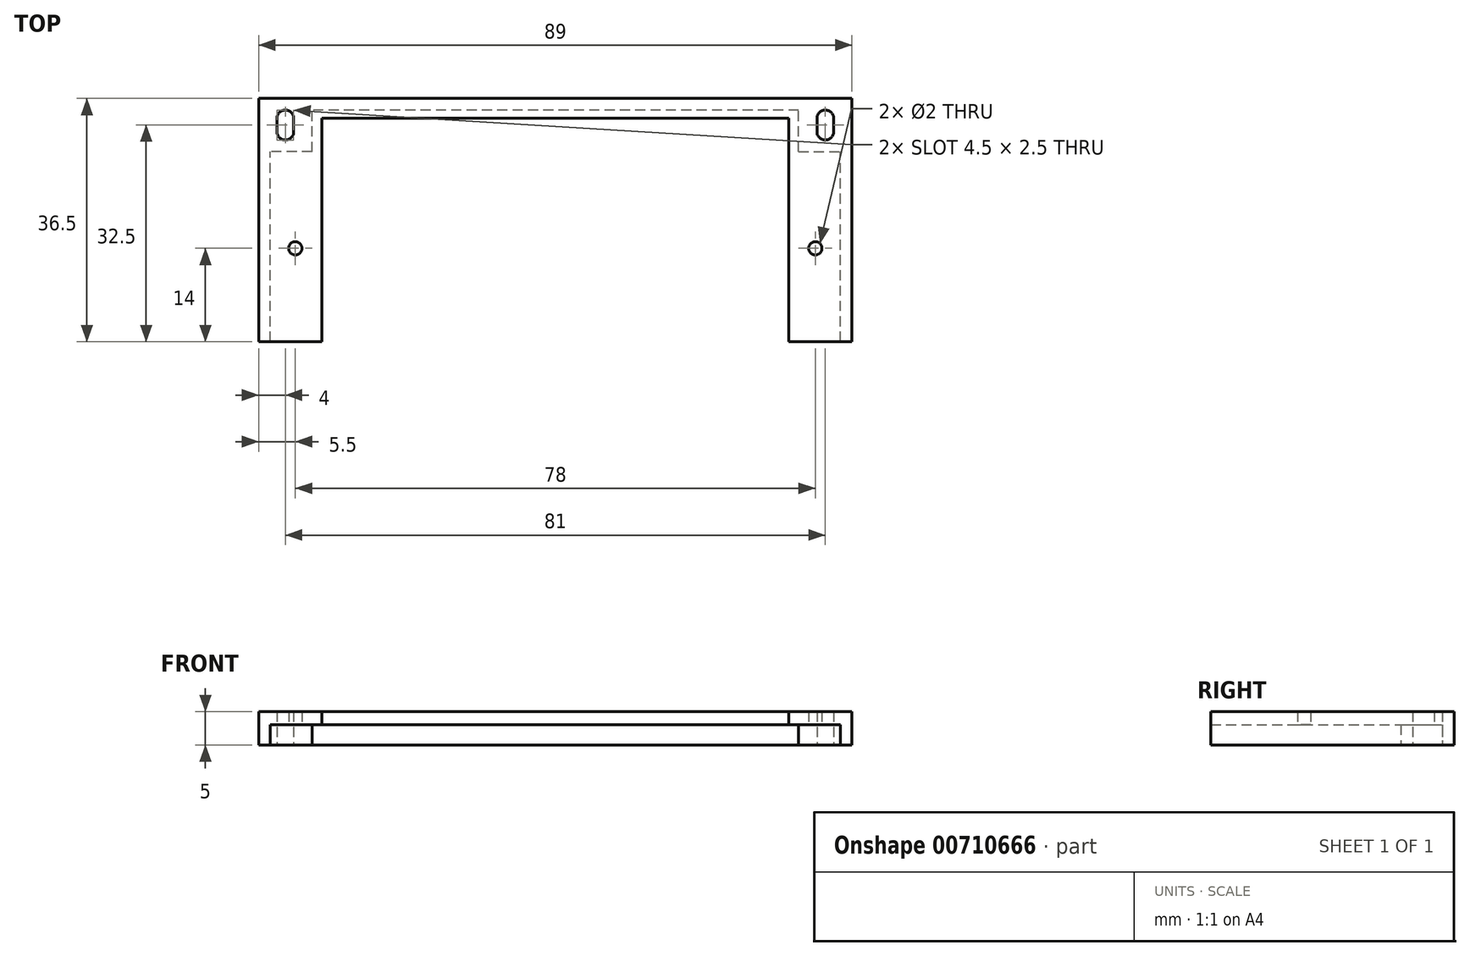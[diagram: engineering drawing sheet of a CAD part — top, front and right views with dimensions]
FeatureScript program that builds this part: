
annotation { "Feature Type Name" : "Feature", "Feature Type Description" : "" }
export const myFeature = defineFeature(function(context is Context, id is Id, definition is map)
    precondition{}
    {
        {
            var Q0;
            Q0=qCreatedBy(makeId("Top.planeOp"),FACE);
            var sketch = newSketch(context, id + "F0", { "sketchPlane" : qUnion([Q0])});
            skLineSegment(sketch, "E0.bottom", {"start": v(44.5, -22.5) * mm, "end": v(-44.5, -22.5) * mm});
            skLineSegment(sketch, "E0.top", {"start": v(44.5, 22.5) * mm, "end": v(-44.5, 22.5) * mm});
            skLineSegment(sketch, "E0.left", {"start": v(44.5, -22.5) * mm, "end": v(44.5, 22.5) * mm});
            skLineSegment(sketch, "E0.right", {"start": v(-44.5, -22.5) * mm, "end": v(-44.5, 22.5) * mm});
            skPoint(sketch, "E0.middle", {"position": v(0, 0) * mm});
            skSolve(sketch);
        }
        {
            var Q0;
            Q0=qSketchRegion(id+"F0",true);
            extrude(context, id + "F1", {"entities" : qUnion([Q0]), "depth" : 5 * mm, "offsetDistance" : 25 * mm});
        }
        {
            var Q0;
            Q0=qCreatedBy(makeId("Top.planeOp"),FACE);
            var sketch = newSketch(context, id + "F2", { "sketchPlane" : qUnion([Q0])});
            skLineSegment(sketch, "E1.bottom", {"start": v(35, -19.5) * mm, "end": v(-35, -19.5) * mm});
            skLineSegment(sketch, "E1.top", {"start": v(35, 19.5) * mm, "end": v(-35, 19.5) * mm});
            skLineSegment(sketch, "E1.left", {"start": v(35, -19.5) * mm, "end": v(35, 19.5) * mm});
            skLineSegment(sketch, "E1.right", {"start": v(-35, -19.5) * mm, "end": v(-35, 19.5) * mm});
            skPoint(sketch, "E1.middle", {"position": v(0, 0) * mm});
            skSolve(sketch);
        }
        {
            var Q0;
            Q0=qSketchRegion(id+"F2",true);
            extrude(context, id + "F3", {"entities" : qUnion([Q0]), "operationType" : NewBodyOperationType.REMOVE, "depth" : 25 * mm, "offsetDistance" : 25 * mm});
        }
        {
            var Q0;
            Q0=qCreatedBy(makeId("Top.planeOp"),FACE);
            var sketch = newSketch(context, id + "F4", { "sketchPlane" : qUnion([Q0])});
            skLineSegment(sketch, "E2.bottom", {"start": v(42.75, -20.75) * mm, "end": v(-42.75, -20.75) * mm});
            skLineSegment(sketch, "E2.top", {"start": v(42.75, 20.75) * mm, "end": v(-42.75, 20.75) * mm});
            skLineSegment(sketch, "E2.left", {"start": v(42.75, -20.75) * mm, "end": v(42.75, 20.75) * mm});
            skLineSegment(sketch, "E2.right", {"start": v(-42.75, -20.75) * mm, "end": v(-42.75, 20.75) * mm});
            skPoint(sketch, "E2.middle", {"position": v(0, 0) * mm});
            skSolve(sketch);
        }
        {
            var Q0;
            Q0=qSketchRegion(id+"F4",true);
            extrude(context, id + "F5", {"entities" : qUnion([Q0]), "operationType" : NewBodyOperationType.REMOVE, "depth" : 3 * mm, "offsetDistance" : 25 * mm});
        }
        {
            var Q0;
            Q0=qCreatedBy(makeId("Top.planeOp"),FACE);
            var sketch = newSketch(context, id + "F6", { "sketchPlane" : qUnion([Q0])});
            skLineSegment(sketch, "E3.bottom", {"start": v(-36.5, 14.5) * mm, "end": v(-44.5, 14.5) * mm});
            skLineSegment(sketch, "E3.top", {"start": v(-36.5, 22.5) * mm, "end": v(-44.5, 22.5) * mm});
            skLineSegment(sketch, "E3.left", {"start": v(-36.5, 14.5) * mm, "end": v(-36.5, 22.5) * mm});
            skLineSegment(sketch, "E3.right", {"start": v(-44.5, 14.5) * mm, "end": v(-44.5, 22.5) * mm});
            skPoint(sketch, "E3.middle", {"position": v(-40.5, 18.5) * mm});
            skLineSegment(sketch, "E4.bottom", {"start": v(-44.5, -22.5) * mm, "end": v(-36.5, -22.5) * mm});
            skLineSegment(sketch, "E4.top", {"start": v(-44.5, -14.5) * mm, "end": v(-36.5, -14.5) * mm});
            skLineSegment(sketch, "E4.left", {"start": v(-44.5, -22.5) * mm, "end": v(-44.5, -14.5) * mm});
            skLineSegment(sketch, "E4.right", {"start": v(-36.5, -22.5) * mm, "end": v(-36.5, -14.5) * mm});
            skPoint(sketch, "E4.middle", {"position": v(-40.5, -18.5) * mm});
            skLineSegment(sketch, "E5.bottom", {"start": v(36.5, 14.5) * mm, "end": v(44.5, 14.5) * mm});
            skLineSegment(sketch, "E5.top", {"start": v(36.5, 22.5) * mm, "end": v(44.5, 22.5) * mm});
            skLineSegment(sketch, "E5.left", {"start": v(36.5, 14.5) * mm, "end": v(36.5, 22.5) * mm});
            skLineSegment(sketch, "E5.right", {"start": v(44.5, 14.5) * mm, "end": v(44.5, 22.5) * mm});
            skPoint(sketch, "E5.middle", {"position": v(40.5, 18.5) * mm});
            skLineSegment(sketch, "E6.bottom", {"start": v(44.5, -14.5) * mm, "end": v(36.5, -14.5) * mm});
            skLineSegment(sketch, "E6.top", {"start": v(44.5, -22.5) * mm, "end": v(36.5, -22.5) * mm});
            skLineSegment(sketch, "E6.left", {"start": v(44.5, -14.5) * mm, "end": v(44.5, -22.5) * mm});
            skLineSegment(sketch, "E6.right", {"start": v(36.5, -14.5) * mm, "end": v(36.5, -22.5) * mm});
            skSolve(sketch);
        }
        {
            var Q0;
            Q0=qSketchRegion(id+"F6",true);
            extrude(context, id + "F7", {"entities" : qUnion([Q0]), "operationType" : NewBodyOperationType.ADD, "depth" : 3 * mm, "offsetDistance" : 25 * mm});
        }
        {
            var Q0;
            Q0=qCreatedBy(makeId("Top.planeOp"),FACE);
            var sketch = newSketch(context, id + "F8", { "sketchPlane" : qUnion([Q0])});
            skCircle(sketch, "E7", {"center": v(40.5, 19.5) * mm, "radius": 1.25 * mm});
            skCircle(sketch, "E8", {"center": v(-40.5, 19.5) * mm, "radius": 1.25 * mm});
            skCircle(sketch, "E9", {"center": v(-39, 0) * mm, "radius": 1 * mm});
            skCircle(sketch, "E10", {"center": v(39, 0) * mm, "radius": 1 * mm});
            skCircle(sketch, "E11.1.0.0", {"center": v(-40.5, 17.5) * mm, "radius": 1.25 * mm});
            skLineSegment(sketch, "E11.direction1", {"start": v(-40.5, 19.5) * mm, "end": v(-40.5, 17.5) * mm, "construction": true});
            skCircle(sketch, "E12.1.0.0", {"center": v(40.5, 17.5) * mm, "radius": 1.25 * mm});
            skLineSegment(sketch, "E12.direction1", {"start": v(40.5, 19.5) * mm, "end": v(40.5, 17.5) * mm, "construction": true});
            skSolve(sketch);
        }
        {
            var Q0;
            Q0=qSketchRegion(id+"F8",true);
            extrude(context, id + "F9", {"entities" : qUnion([Q0]), "operationType" : NewBodyOperationType.REMOVE, "depth" : 25 * mm, "offsetDistance" : 25 * mm});
        }
        {
            var Q0;
            Q0=qSketchRegion(id+"F8",true);
            extrude(context, id + "F10", {"entities" : qUnion([Q0]), "operationType" : NewBodyOperationType.REMOVE, "depth" : 25 * mm, "offsetDistance" : 25 * mm});
        }
        {
            var Q0;
            Q0=makeQuery(id+"F7.boolean.opBoolean","MERGE",FACE,{"derivedFrom":[makeQuery(id+"F1.opExtrude","CAP_FACE",FACE,{"disambiguationData":[OSD([sQuery(id+"F0.wireOp",EDGE,"E0.bottom"),sQuery(id+"F0.wireOp",EDGE,"E0.top"),sQuery(id+"F0.wireOp",EDGE,"E0.left"),sQuery(id+"F0.wireOp",EDGE,"E0.right")])],"isStart":true}),makeQuery(id+"F7.opExtrude","CAP_FACE",FACE,{"disambiguationData":[OSD([sQuery(id+"F6.wireOp",EDGE,"E3.bottom"),sQuery(id+"F6.wireOp",EDGE,"E3.top"),sQuery(id+"F6.wireOp",EDGE,"E3.left"),sQuery(id+"F6.wireOp",EDGE,"E3.right")])],"isStart":true}),makeQuery(id+"F7.opExtrude","CAP_FACE",FACE,{"disambiguationData":[OSD([sQuery(id+"F6.wireOp",EDGE,"E4.bottom"),sQuery(id+"F6.wireOp",EDGE,"E4.top"),sQuery(id+"F6.wireOp",EDGE,"E4.left"),sQuery(id+"F6.wireOp",EDGE,"E4.right")])],"isStart":true}),makeQuery(id+"F7.opExtrude","CAP_FACE",FACE,{"disambiguationData":[OSD([sQuery(id+"F6.wireOp",EDGE,"E5.bottom"),sQuery(id+"F6.wireOp",EDGE,"E5.top"),sQuery(id+"F6.wireOp",EDGE,"E5.left"),sQuery(id+"F6.wireOp",EDGE,"E5.right")])],"isStart":true}),makeQuery(id+"F7.opExtrude","CAP_FACE",FACE,{"disambiguationData":[OSD([sQuery(id+"F6.wireOp",EDGE,"E6.bottom"),sQuery(id+"F6.wireOp",EDGE,"E6.top"),sQuery(id+"F6.wireOp",EDGE,"E6.left"),sQuery(id+"F6.wireOp",EDGE,"E6.right")])],"isStart":true})]});
            var sketch = newSketch(context, id + "F11", { "sketchPlane" : qUnion([Q0])});
            skLineSegment(sketch, "E13.bottom", {"start": v(-41.75, -19.5) * mm, "end": v(-39.25, -19.5) * mm});
            skLineSegment(sketch, "E13.top", {"start": v(-41.75, -17.5) * mm, "end": v(-39.25, -17.5) * mm});
            skLineSegment(sketch, "E13.left", {"start": v(-41.75, -19.5) * mm, "end": v(-41.75, -17.5) * mm});
            skLineSegment(sketch, "E13.right", {"start": v(-39.25, -19.5) * mm, "end": v(-39.25, -17.5) * mm});
            skLineSegment(sketch, "E14.bottom", {"start": v(39.25, -19.5) * mm, "end": v(41.75, -19.5) * mm});
            skLineSegment(sketch, "E14.top", {"start": v(39.25, -17.5) * mm, "end": v(41.75, -17.5) * mm});
            skLineSegment(sketch, "E14.left", {"start": v(39.25, -19.5) * mm, "end": v(39.25, -17.5) * mm});
            skLineSegment(sketch, "E14.right", {"start": v(41.75, -19.5) * mm, "end": v(41.75, -17.5) * mm});
            skSolve(sketch);
        }
        {
            var Q0;
            Q0=qSketchRegion(id+"F11",true);
            extrude(context, id + "F12", {"entities" : qUnion([Q0]), "operationType" : NewBodyOperationType.REMOVE, "oppositeDirection" : true, "depth" : 25 * mm, "offsetDistance" : 25 * mm});
        }
        {
            var Q0;
            Q0=makeQuery(id+"F1.opExtrude","CAP_FACE",FACE,{"disambiguationData":[OSD([sQuery(id+"F0.wireOp",EDGE,"E0.bottom"),sQuery(id+"F0.wireOp",EDGE,"E0.top"),sQuery(id+"F0.wireOp",EDGE,"E0.left"),sQuery(id+"F0.wireOp",EDGE,"E0.right")])],"isStart":false});
            var sketch = newSketch(context, id + "F13", { "sketchPlane" : qUnion([Q0])});
            skLineSegment(sketch, "E15.bottom", {"start": v(44.5, -22.5) * mm, "end": v(-44.5, -22.5) * mm});
            skLineSegment(sketch, "E15.top", {"start": v(44.5, -14) * mm, "end": v(-44.5, -14) * mm});
            skLineSegment(sketch, "E15.left", {"start": v(44.5, -22.5) * mm, "end": v(44.5, -14) * mm});
            skLineSegment(sketch, "E15.right", {"start": v(-44.5, -22.5) * mm, "end": v(-44.5, -14) * mm});
            skSolve(sketch);
        }
        {
            var Q0;
            Q0=qSketchRegion(id+"F13",true);
            extrude(context, id + "F14", {"entities" : qUnion([Q0]), "operationType" : NewBodyOperationType.REMOVE, "oppositeDirection" : true, "depth" : 25 * mm, "offsetDistance" : 25 * mm});
        }
    });
